# Revit family: Chair-Multi_Purpose-Allermuir-Tonina-TN1U
name_source: partatom
category: Furniture
revit_build: Autodesk Revit MEP 2012 (Build: 20110309_2315)
units: mm (PartAtom-declared; Revit-internal decimal feet)

## types (1)
- TN1U
    04 CSI = 12 51 00
    95 CSI = 12510
    Arms Height = 0"
    Assembly Code = E2020200
    Color Availability = See price list for material options
    Default Elevation = 48"
    Fabric Spec Sheets = http://www.allermuir.net
    Manufacturer = Allermuir
    Manufacturer Fax = (419) 887 5805
    Model = TN1U
    Overall Depth = 22 5/256"
    Overall Height = 32 1/32"
    Overall Width = 19 239/256"
    Plugin Data URL = http://products.ecoscorecard.com
    Product Line = Tonina
    Seat = Plastic  - Allermuir - Black - Smooth
    Seat Depth = 0"
    Seat Height = 15 3/4"
    Seat Width = 26"
    Seat or Base = Plastic  - Allermuir - Black - Smooth
    Stacks = Yes
    Subcategory = Multi-Purpose Line
    URL = http://www.allermuir.net
    Weight = 0.00 kN
    ecoScorecard Product Page = http://products.ecoscorecard.com
    ecoScorecard_data = http://thesenatorgroup.ecoscorecard.com

## geometry (parser evidence)
native form markers: Blend x4, Sweep x2
no freeform markers — native parametric forms only
